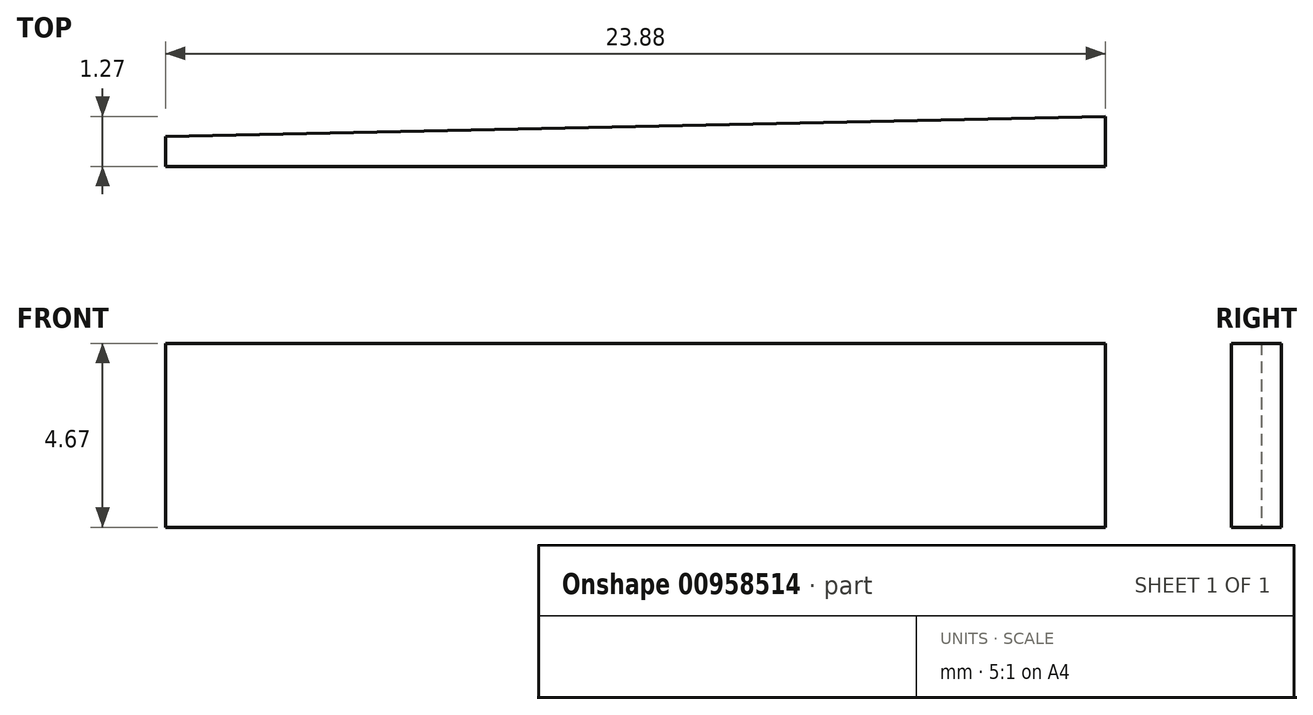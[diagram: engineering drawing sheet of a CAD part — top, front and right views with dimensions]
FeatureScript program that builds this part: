
annotation { "Feature Type Name" : "Feature", "Feature Type Description" : "" }
export const myFeature = defineFeature(function(context is Context, id is Id, definition is map)
    precondition{}
    {
        {
            var Q0;
            Q0=qCreatedBy(makeId("Top.planeOp"),FACE);
            var sketch = newSketch(context, id + "F0", { "sketchPlane" : qUnion([Q0])});
            skLineSegment(sketch, "E0", {"start": v(0, 0) * mm, "end": v(23.88, 0) * mm});
            skLineSegment(sketch, "E1", {"start": v(23.88, 0) * mm, "end": v(23.88, 1.27) * mm});
            skLineSegment(sketch, "E2", {"start": v(0, 0) * mm, "end": v(0, 0.76) * mm});
            skLineSegment(sketch, "E3", {"start": v(23.88, 1.27) * mm, "end": v(0, 0.76) * mm});
            skSolve(sketch);
        }
        {
            var Q0;
            Q0=makeQuery(id+"F0.imprint","IMPRINT",FACE,{"disambiguationData":[TD([[makeQuery(id+"F0.imprint","IMPRINT",EDGE,{"derivedFrom":sQuery(id+"F0.wireOp",EDGE,"E0")}),1.0]])]});
            extrude(context, id + "F1", {"entities" : qUnion([Q0]), "depth" : 4.67 * mm, "offsetDistance" : 25.4 * mm});
        }
    });
